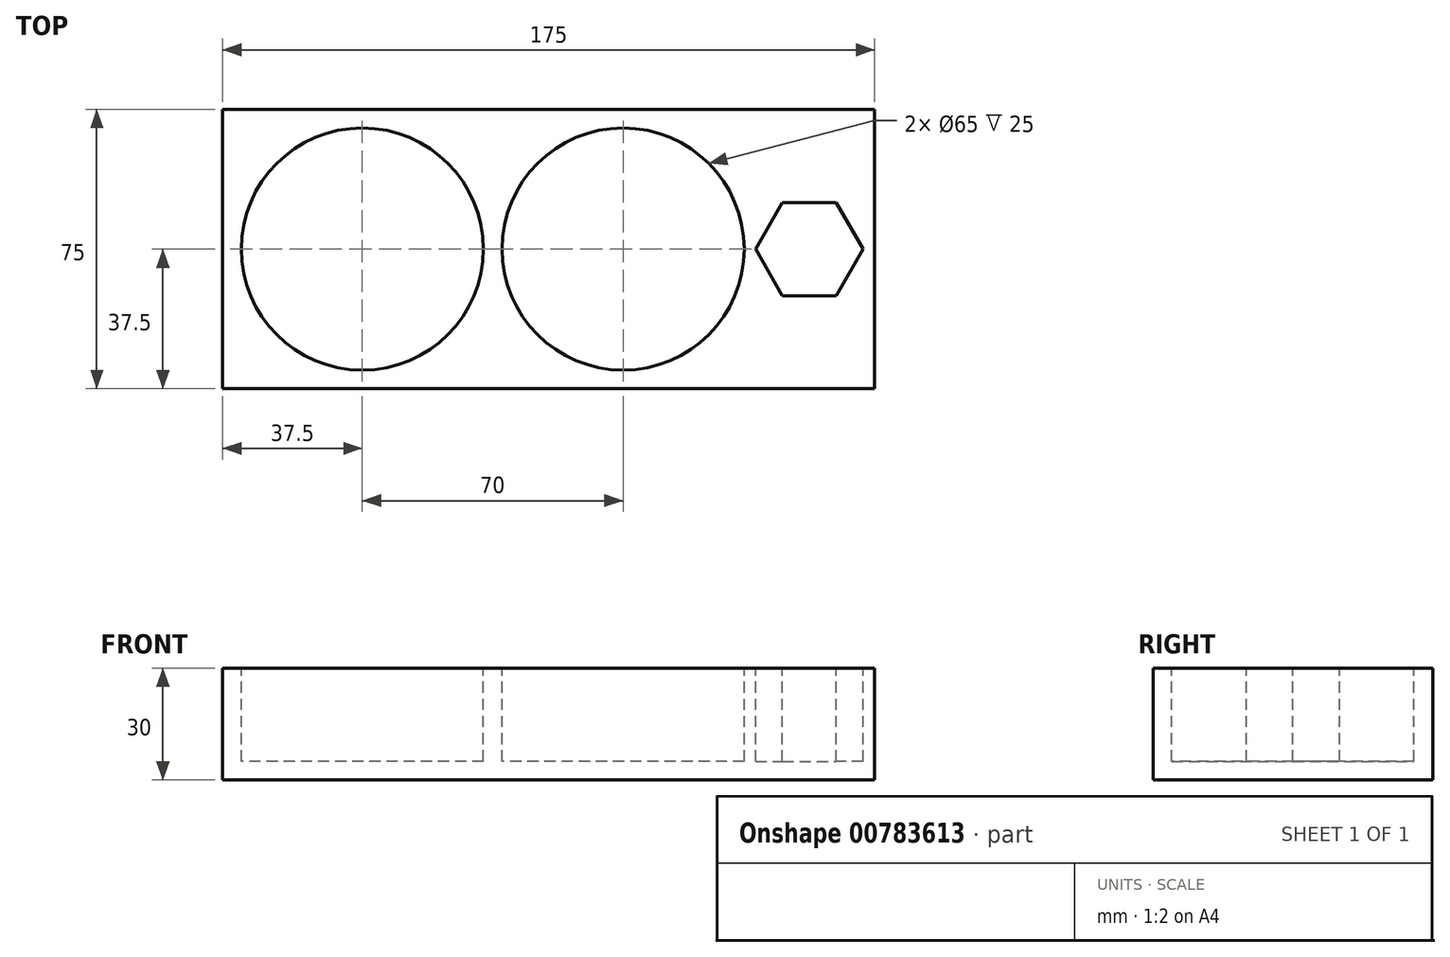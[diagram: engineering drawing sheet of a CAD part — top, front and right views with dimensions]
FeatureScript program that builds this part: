
annotation { "Feature Type Name" : "Feature", "Feature Type Description" : "" }
export const myFeature = defineFeature(function(context is Context, id is Id, definition is map)
    precondition{}
    {
        {
            var Q0;
            Q0=qCreatedBy(makeId("Top.planeOp"),FACE);
            var sketch = newSketch(context, id + "F0", { "sketchPlane" : qUnion([Q0])});
            skLineSegment(sketch, "E0.bottom", {"start": v(87.5, -37.5) * mm, "end": v(-87.5, -37.5) * mm});
            skLineSegment(sketch, "E0.top", {"start": v(87.5, 37.5) * mm, "end": v(-87.5, 37.5) * mm});
            skLineSegment(sketch, "E0.left", {"start": v(87.5, -37.5) * mm, "end": v(87.5, 37.5) * mm});
            skLineSegment(sketch, "E0.right", {"start": v(-87.5, -37.5) * mm, "end": v(-87.5, 37.5) * mm});
            skPoint(sketch, "E0.middle", {"position": v(0, 0) * mm});
            skPoint(sketch, "E1", {"position": v(-50.89, 0) * mm});
            skPoint(sketch, "E2", {"position": v(-10.82, 0) * mm});
            skPoint(sketch, "E3", {"position": v(37.06, 0) * mm});
            skSolve(sketch);
        }
        {
            var Q0;
            Q0 = qSketchRegion(id + "F0", true);
            extrude(context, id + "F1", {"entities" : qUnion([Q0]), "depth" : 30 * mm, "offsetDistance" : 25 * mm});
        }
        {
            var Q0;
            Q0=makeQuery(id+"F1.opExtrude","CAP_FACE",FACE,{"disambiguationData":[OSD([sQuery(id+"F0.wireOp",EDGE,"E0.bottom"),sQuery(id+"F0.wireOp",EDGE,"E0.top"),sQuery(id+"F0.wireOp",EDGE,"E0.left"),sQuery(id+"F0.wireOp",EDGE,"E0.right")])],"isStart":false});
            var sketch = newSketch(context, id + "F2", { "sketchPlane" : qUnion([Q0])});
            skLineSegment(sketch, "E4", {"start": v(-87.5, 0) * mm, "end": v(87.5, 0) * mm, "construction": true});
            skPoint(sketch, "E5", {"position": v(-50, 0) * mm});
            skPoint(sketch, "E6", {"position": v(20, 0) * mm});
            skPoint(sketch, "E7", {"position": v(70, 0) * mm});
            skCircle(sketch, "E8", {"center": v(-50, 0) * mm, "radius": 32.5 * mm});
            skCircle(sketch, "E9", {"center": v(20, 0) * mm, "radius": 32.5 * mm});
            skCircle(sketch, "E10.cCircle", {"center": v(70, 0) * mm, "radius": 12.5 * mm, "construction": true});
            skLineSegment(sketch, "E10.0", {"start": v(84.43, 0) * mm, "end": v(77.22, -12.5) * mm});
            skLineSegment(sketch, "E10.1", {"start": v(77.22, -12.5) * mm, "end": v(62.78, -12.5) * mm});
            skLineSegment(sketch, "E10.2", {"start": v(62.78, -12.5) * mm, "end": v(55.57, 0) * mm});
            skLineSegment(sketch, "E10.3", {"start": v(55.57, 0) * mm, "end": v(62.78, 12.5) * mm});
            skLineSegment(sketch, "E10.4", {"start": v(62.78, 12.5) * mm, "end": v(77.22, 12.5) * mm});
            skLineSegment(sketch, "E10.5", {"start": v(77.22, 12.5) * mm, "end": v(84.43, 0) * mm});
            skPoint(sketch, "E10.0.midPoint", {"position": v(80.83, -6.25) * mm});
            skSolve(sketch);
        }
        {
            var Q0;
            Q0 = qSketchRegion(id + "F2", true);
            extrude(context, id + "F3", {"entities" : qUnion([Q0]), "operationType" : NewBodyOperationType.REMOVE, "oppositeDirection" : true, "depth" : 25 * mm, "offsetDistance" : 25 * mm});
        }
    });
